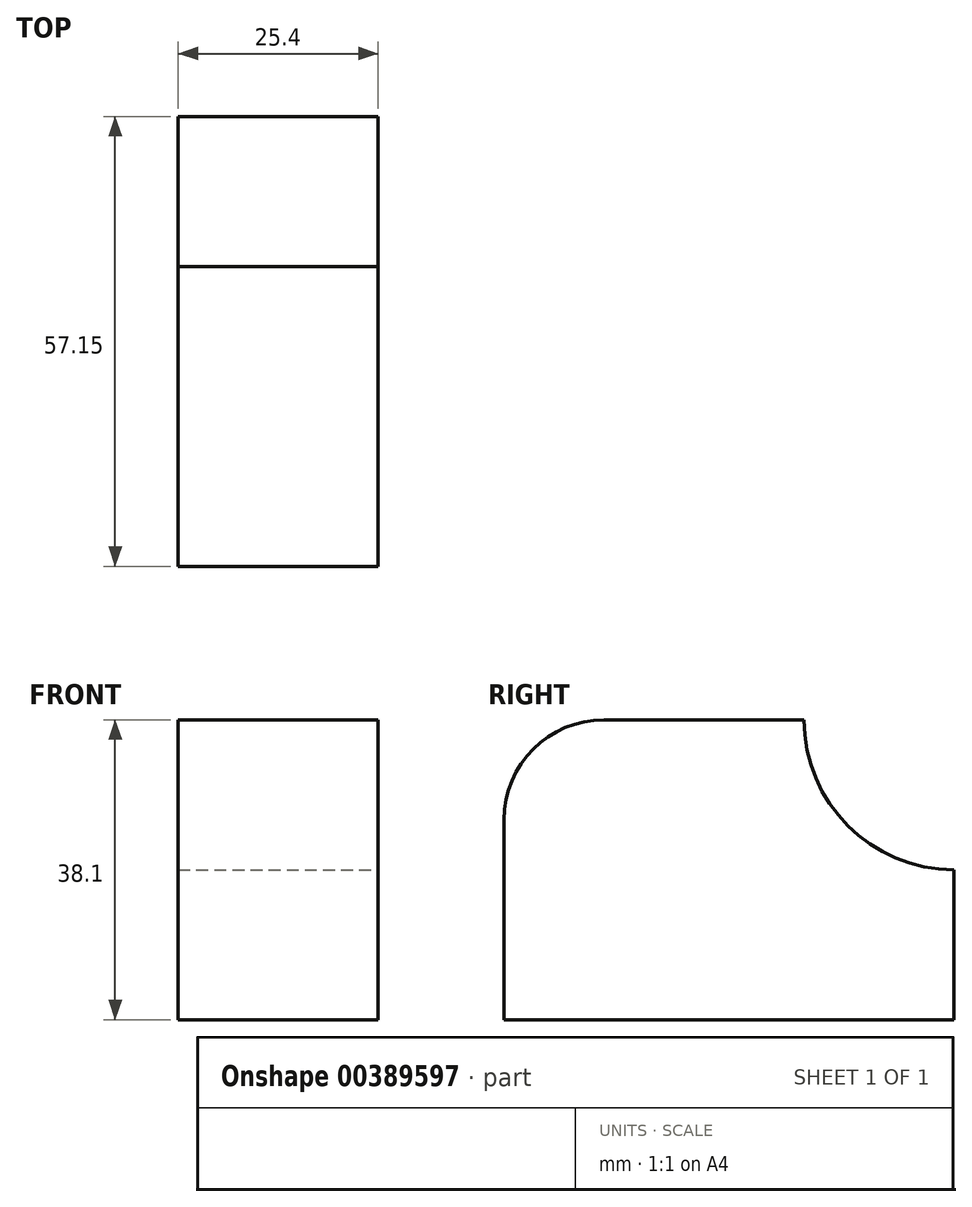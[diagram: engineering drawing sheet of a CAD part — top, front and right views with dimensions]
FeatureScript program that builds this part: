
annotation { "Feature Type Name" : "Feature", "Feature Type Description" : "" }
export const myFeature = defineFeature(function(context is Context, id is Id, definition is map)
    precondition{}
    {
        {
            var Q0;
            Q0=qCreatedBy(makeId("Right.planeOp"),FACE);
            var sketch = newSketch(context, id + "F0", { "sketchPlane" : qUnion([Q0])});
            skLineSegment(sketch, "E0", {"start": v(0, 0) * mm, "end": v(57.15, 0) * mm});
            skLineSegment(sketch, "E1", {"start": v(57.15, 0) * mm, "end": v(57.15, 38.1) * mm});
            skLineSegment(sketch, "E2", {"start": v(57.15, 38.1) * mm, "end": v(0, 38.1) * mm});
            skLineSegment(sketch, "E3", {"start": v(0, 38.1) * mm, "end": v(0, 0) * mm});
            skSolve(sketch);
        }
        {
            var Q0;
            Q0=makeQuery(id+"F0.imprint","IMPRINT",FACE,{"disambiguationData":[TD([[makeQuery(id+"F0.imprint","IMPRINT",EDGE,{"derivedFrom":sQuery(id+"F0.wireOp",EDGE,"E0")}),1.0]])]});
            extrude(context, id + "F1", {"entities" : qUnion([Q0]), "depth" : 25.4 * mm});
        }
        {
            var Q0;
            Q0=makeQuery(id+"F1.opExtrude","SWEPT_EDGE",EDGE,{"disambiguationData":[OSD([sQuery(id+"F0.wireOp",EDGE,"E2"),sQuery(id+"F0.wireOp",EDGE,"E3")])]});
            fillet(context, id + "F2", {"entities" : qUnion([Q0]), "radius" : 12.7 * mm, "tangentPropagation" : true, "allowEdgeOverflow" : false});
        }
        {
            var Q0;
            Q0=makeQuery(id+"F1.opExtrude","CAP_FACE",FACE,{"disambiguationData":[OSD([sQuery(id+"F0.wireOp",EDGE,"E0"),sQuery(id+"F0.wireOp",EDGE,"E1"),sQuery(id+"F0.wireOp",EDGE,"E2"),sQuery(id+"F0.wireOp",EDGE,"E3")])],"isStart":false});
            var sketch = newSketch(context, id + "F3", { "sketchPlane" : qUnion([Q0])});
            skCircle(sketch, "E4", {"center": v(57.15, 38.1) * mm, "radius": 19.05 * mm});
            skSolve(sketch);
        }
        {
            var Q0;
            {var subQ0=sQuery(id+"F3.wireOp",EDGE,"E4");var subQ1=makeQuery(id+"F1.opExtrude","CAP_EDGE",EDGE,{"disambiguationData":[OSD([sQuery(id+"F0.wireOp",EDGE,"E1")])],"isStart":false});var subQ2=makeQuery(id+"F3.imprint","INTERSECT",VERTEX,{"derivedFrom":[subQ1,subQ0]});Q0=makeQuery(id+"F3.imprint","IMPRINT",FACE,{"disambiguationData":[TD([[makeQuery(id+"F3.imprint","IMPRINT",EDGE,{"disambiguationData":[TD([[subQ2,1.0]])],"derivedFrom":subQ0}),1.0]])]});}
            extrude(context, id + "F4", {"entities" : qUnion([Q0]), "operationType" : NewBodyOperationType.REMOVE, "oppositeDirection" : true, "depth" : 25.4 * mm});
        }
    });
